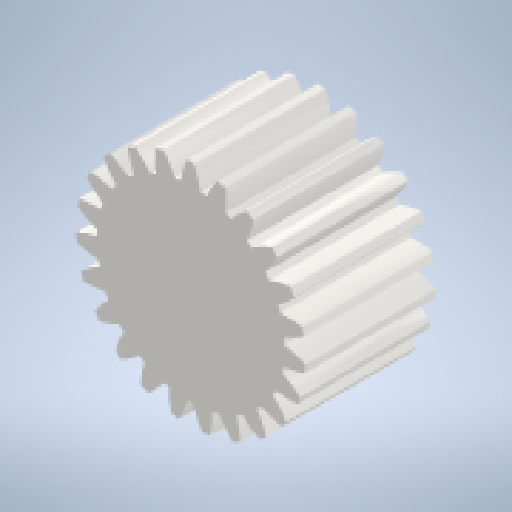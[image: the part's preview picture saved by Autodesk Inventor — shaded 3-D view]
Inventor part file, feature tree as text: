
AUTODESK INVENTOR PART (.ipt)
format: ipt  version: 2023.2 (Build 272271000, 271)  size: 268,800 bytes
history: native  units: mm (DEFAULTED — no unit token found)
features: plane x3, other x3, sketch x3, extrude x2
ambient origin geometry x8: Origin, YZ Plane, XZ Plane, XY Plane, X Axis, Y Axis, Z Axis, Center Point
bodies: Solid1 (feature_tree)
feature tree (11):
  extrude  "Extrusion1"  Depth=5.0mm TaperAngle=0.0deg
  plane  "Work Plane2"
  plane  "Work Plane8"
  plane  "Work Plane9"
  other  "Spur Gear"
  extrude  "Extrusion2"  Depth=10.0mm TaperAngle=0.0deg
  sketch  "Sketch1"  dims[d0=17.506247mm d1=5.0mm d2=0.0mm]
  sketch  "Sketch2"  dims[d3=16.1mm d4=10.0mm d5=0.0mm]
  other  "Srf1"
  sketch  "Sketch3"  dims[d16=12.604893mm d17=0.0mm d34=1.36591mm d39=0.0mm d41=0.0mm d43=12.604893mm d46=12.604893mm d47=0.0mm d48=0.0mm d49=1.0mm d50=100.0mm d51=0.0mm]
  other  "Pitch Diameter"
